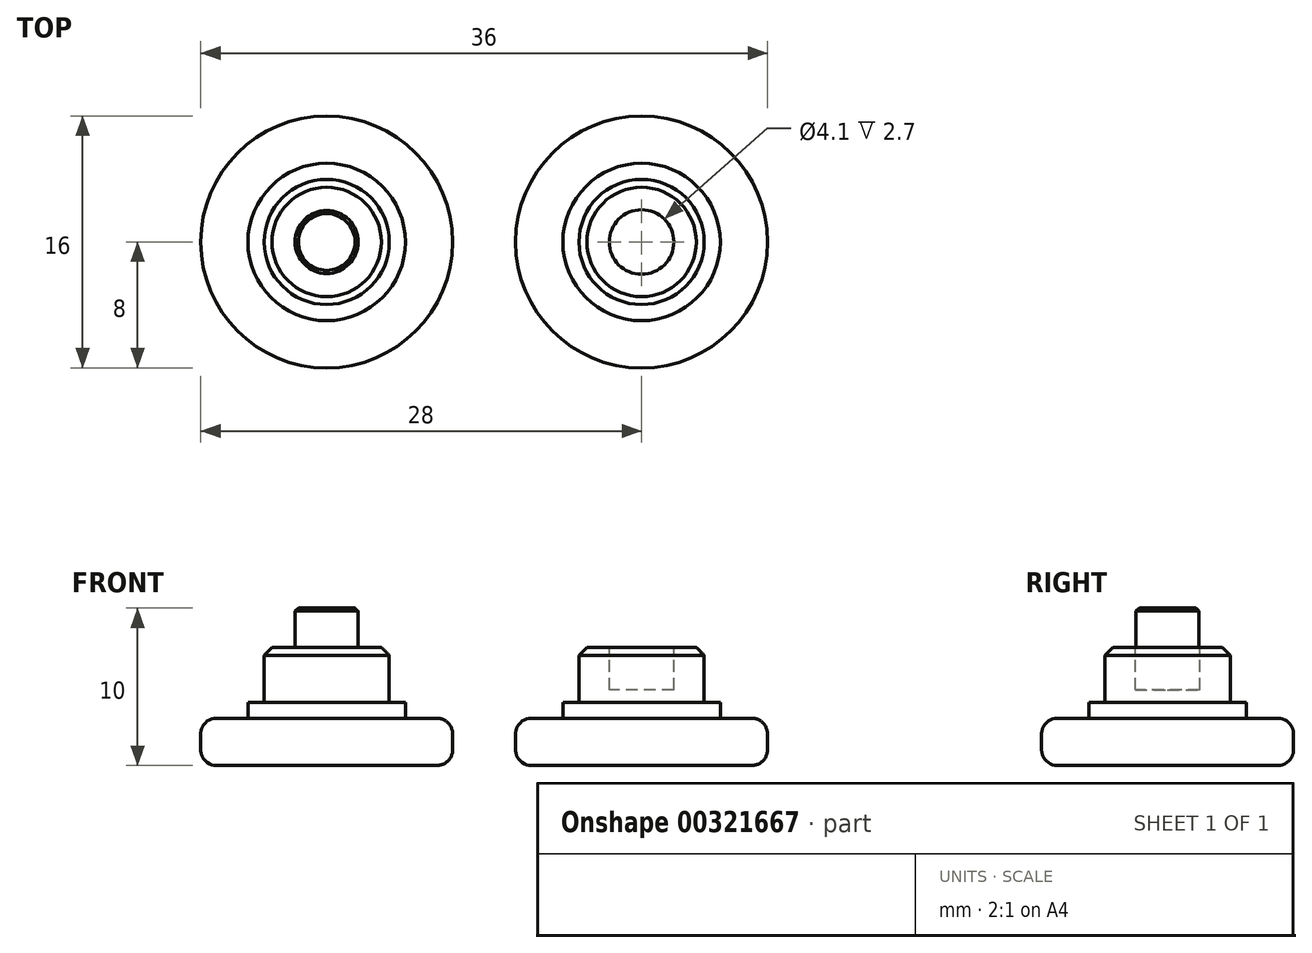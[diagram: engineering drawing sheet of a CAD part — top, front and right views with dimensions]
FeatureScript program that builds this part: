
annotation { "Feature Type Name" : "Feature", "Feature Type Description" : "" }
export const myFeature = defineFeature(function(context is Context, id is Id, definition is map)
    precondition{}
    {
        {
            var Q0;
            Q0=qCreatedBy(makeId("Top.planeOp"),FACE);
            var sketch = newSketch(context, id + "F0", { "sketchPlane" : qUnion([Q0])});
            skCircle(sketch, "E0", {"center": v(0, 0) * mm, "radius": 8 * mm});
            skSolve(sketch);
        }
        {
            var Q0;
            Q0=makeQuery(id+"F0.imprint","IMPRINT",FACE,{"disambiguationData":[TD([[makeQuery(id+"F0.imprint","IMPRINT",EDGE,{"derivedFrom":sQuery(id+"F0.wireOp",EDGE,"E0")}),1.0]])]});
            extrude(context, id + "F1", {"entities" : qUnion([Q0]), "depth" : 3 * mm});
        }
        {
            var Q0;
            Q0=makeQuery(id+"F1.opExtrude","CAP_FACE",FACE,{"disambiguationData":[OSD([sQuery(id+"F0.wireOp",EDGE,"E0")])],"isStart":false});
            var sketch = newSketch(context, id + "F2", { "sketchPlane" : qUnion([Q0])});
            skCircle(sketch, "E1", {"center": v(0, 0) * mm, "radius": 5 * mm});
            skSolve(sketch);
        }
        {
            var Q0;
            Q0=makeQuery(id+"F2.imprint","IMPRINT",FACE,{"disambiguationData":[TD([[makeQuery(id+"F2.imprint","IMPRINT",EDGE,{"derivedFrom":sQuery(id+"F2.wireOp",EDGE,"E1")}),1.0]])]});
            extrude(context, id + "F3", {"entities" : qUnion([Q0]), "operationType" : NewBodyOperationType.ADD, "depth" : 1 * mm});
        }
        {
            var Q0;
            Q0=makeQuery(id+"F3.opExtrude","CAP_FACE",FACE,{"disambiguationData":[OSD([sQuery(id+"F2.wireOp",EDGE,"E1")])],"isStart":false});
            var sketch = newSketch(context, id + "F4", { "sketchPlane" : qUnion([Q0])});
            skCircle(sketch, "E2", {"center": v(0, 0) * mm, "radius": 3.98 * mm});
            skSolve(sketch);
        }
        {
            var Q0;
            Q0=makeQuery(id+"F4.imprint","IMPRINT",FACE,{"disambiguationData":[TD([[makeQuery(id+"F4.imprint","IMPRINT",EDGE,{"derivedFrom":sQuery(id+"F4.wireOp",EDGE,"E2")}),1.0]])]});
            extrude(context, id + "F5", {"entities" : qUnion([Q0]), "operationType" : NewBodyOperationType.ADD, "depth" : 3.5 * mm});
        }
        {
            var Q0;
            Q0=qCreatedBy(makeId("Right.planeOp"),FACE);
            cPlane(context, id + "F6", {"entities" : qUnion([Q0]), "cplaneType" : CPlaneType.OFFSET, "offset" : 10 * mm, "width" : 150 * mm, "height" : 150 * mm});
        }
        {
            var Q0;
            Q0=makeQuery(id+"F1.opExtrude","SWEPT_BODY",BODY,{"disambiguationData":[OSD([sQuery(id+"F0.wireOp",EDGE,"E0")])]});
            var Q1;
            Q1=qCreatedBy(id+"F6.planeOp",FACE);
            mirror(context, id + "F7", {"entities" : qUnion([Q0]), "mirrorPlane" : qUnion([Q1])});
        }
        {
            var Q0;
            Q0=makeQuery(id+"F5.opExtrude","CAP_FACE",FACE,{"disambiguationData":[OSD([sQuery(id+"F4.wireOp",EDGE,"E2")])],"isStart":false});
            var sketch = newSketch(context, id + "F8", { "sketchPlane" : qUnion([Q0])});
            skCircle(sketch, "E3", {"center": v(0, 0) * mm, "radius": 2 * mm});
            skSolve(sketch);
        }
        {
            var Q0;
            Q0=makeQuery(id+"F8.imprint","IMPRINT",FACE,{"disambiguationData":[TD([[makeQuery(id+"F8.imprint","IMPRINT",EDGE,{"derivedFrom":sQuery(id+"F8.wireOp",EDGE,"E3")}),1.0]])]});
            extrude(context, id + "F9", {"entities" : qUnion([Q0]), "operationType" : NewBodyOperationType.ADD, "depth" : 2.5 * mm});
        }
        {
            var Q0;
            Q0=makeQuery(id+"F7.opPattern","COPY",FACE,{"derivedFrom":makeQuery(id+"F5.opExtrude","CAP_FACE",FACE,{"disambiguationData":[OSD([sQuery(id+"F4.wireOp",EDGE,"E2")])],"isStart":false}),"instanceName":"1"});
            var sketch = newSketch(context, id + "F10", { "sketchPlane" : qUnion([Q0])});
            skCircle(sketch, "E4", {"center": v(20, 0) * mm, "radius": 2.05 * mm});
            skSolve(sketch);
        }
        {
            var Q0;
            Q0=makeQuery(id+"F10.imprint","IMPRINT",FACE,{"disambiguationData":[TD([[makeQuery(id+"F10.imprint","IMPRINT",EDGE,{"derivedFrom":sQuery(id+"F10.wireOp",EDGE,"E4")}),1.0]])]});
            extrude(context, id + "F11", {"entities" : qUnion([Q0]), "operationType" : NewBodyOperationType.REMOVE, "oppositeDirection" : true, "depth" : 2.7 * mm});
        }
        {
            var Q0;
            Q0=makeQuery(id+"F9.opExtrude","CAP_EDGE",EDGE,{"disambiguationData":[OSD([sQuery(id+"F8.wireOp",EDGE,"E3")])],"isStart":false});
            chamfer(context, id + "F12", {"entities" : qUnion([Q0]), "width" : 0.2 * mm, "tangentPropagation" : true});
        }
        {
            var Q0;
            Q0=makeQuery(id+"F5.opExtrude","CAP_EDGE",EDGE,{"disambiguationData":[OSD([sQuery(id+"F4.wireOp",EDGE,"E2")])],"isStart":false});
            var Q1;
            Q1=makeQuery(id+"F7.opPattern","COPY",EDGE,{"derivedFrom":makeQuery(id+"F5.opExtrude","CAP_EDGE",EDGE,{"disambiguationData":[OSD([sQuery(id+"F4.wireOp",EDGE,"E2")])],"isStart":false}),"instanceName":"1"});
            chamfer(context, id + "F13", {"entities" : qUnion([Q0, Q1]), "width" : 0.5 * mm, "tangentPropagation" : true});
        }
        {
            var Q0;
            Q0=makeQuery(id+"F1.opExtrude","CAP_EDGE",EDGE,{"disambiguationData":[OSD([sQuery(id+"F0.wireOp",EDGE,"E0")])],"isStart":false});
            var Q1;
            Q1=makeQuery(id+"F7.opPattern","COPY",EDGE,{"derivedFrom":makeQuery(id+"F1.opExtrude","CAP_EDGE",EDGE,{"disambiguationData":[OSD([sQuery(id+"F0.wireOp",EDGE,"E0")])],"isStart":false}),"instanceName":"1"});
            var Q2;
            Q2=makeQuery(id+"F7.opPattern","COPY",EDGE,{"derivedFrom":makeQuery(id+"F1.opExtrude","CAP_EDGE",EDGE,{"disambiguationData":[OSD([sQuery(id+"F0.wireOp",EDGE,"E0")])],"isStart":true}),"instanceName":"1"});
            var Q3;
            Q3=makeQuery(id+"F1.opExtrude","CAP_EDGE",EDGE,{"disambiguationData":[OSD([sQuery(id+"F0.wireOp",EDGE,"E0")])],"isStart":true});
            fillet(context, id + "F14", {"entities" : qUnion([Q0, Q1, Q2, Q3]), "radius" : 1 * mm, "tangentPropagation" : true, "allowEdgeOverflow" : false});
        }
    });
